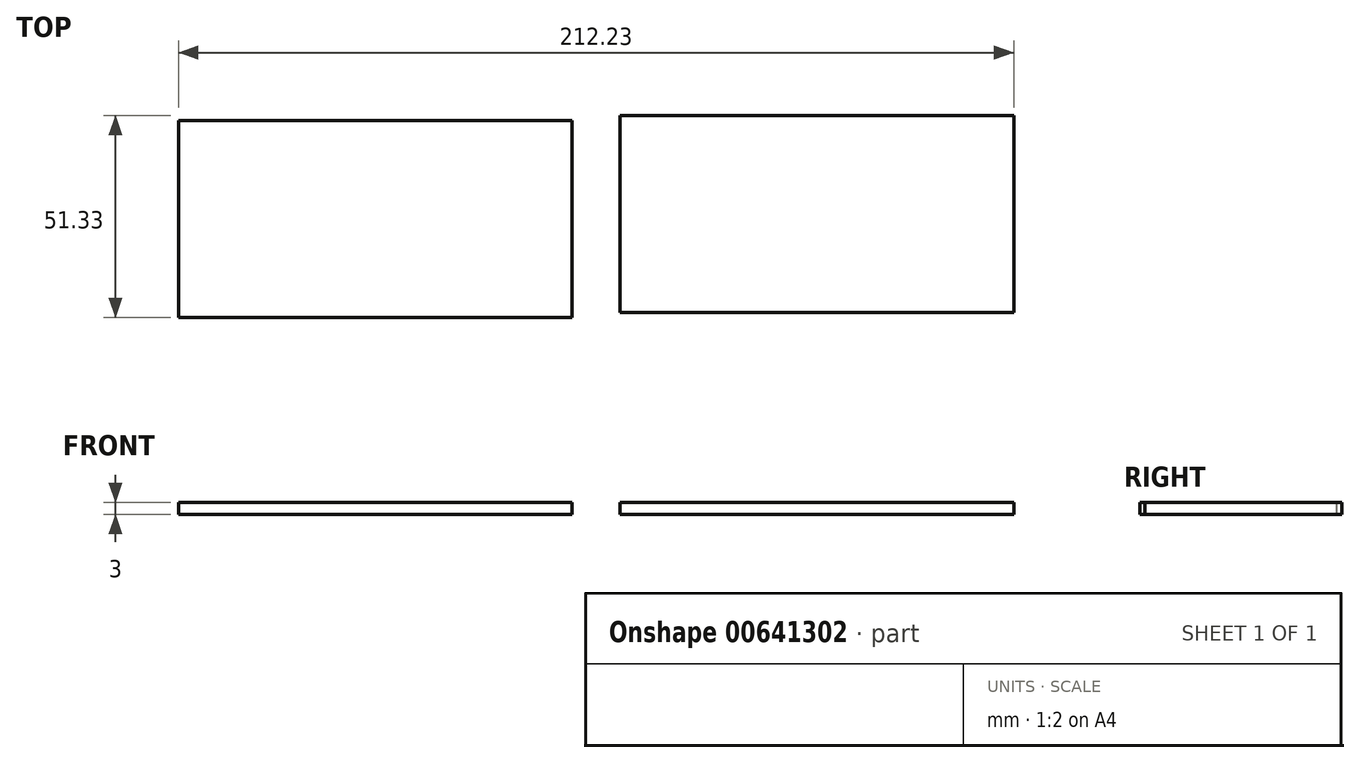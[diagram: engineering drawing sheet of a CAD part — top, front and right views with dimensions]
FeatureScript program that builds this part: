
annotation { "Feature Type Name" : "Feature", "Feature Type Description" : "" }
export const myFeature = defineFeature(function(context is Context, id is Id, definition is map)
    precondition{}
    {
        {
            var Q0;
            Q0=qCreatedBy(makeId("Top.planeOp"),FACE);
            var sketch = newSketch(context, id + "F0", { "sketchPlane" : qUnion([Q0])});
            skLineSegment(sketch, "E0.bottom", {"start": v(0, 0) * mm, "end": v(-100, 0) * mm});
            skLineSegment(sketch, "E0.top", {"start": v(0, 50) * mm, "end": v(-100, 50) * mm});
            skLineSegment(sketch, "E0.left", {"start": v(0, 0) * mm, "end": v(0, 50) * mm});
            skLineSegment(sketch, "E0.right", {"start": v(-100, 0) * mm, "end": v(-100, 50) * mm});
            skLineSegment(sketch, "E1.bottom", {"start": v(12.23, 1.33) * mm, "end": v(112.23, 1.33) * mm});
            skLineSegment(sketch, "E1.top", {"start": v(12.23, 51.33) * mm, "end": v(112.23, 51.33) * mm});
            skLineSegment(sketch, "E1.left", {"start": v(12.23, 1.33) * mm, "end": v(12.23, 51.33) * mm});
            skLineSegment(sketch, "E1.right", {"start": v(112.23, 1.33) * mm, "end": v(112.23, 51.33) * mm});
            skLineSegment(sketch, "E2.bottom", {"start": v(-28.72, -4.26) * mm, "end": v(-28.72, -4.26) * mm});
            skLineSegment(sketch, "E2.top", {"start": v(-28.72, -4.26) * mm, "end": v(-28.72, -4.26) * mm});
            skLineSegment(sketch, "E2.left", {"start": v(-28.72, -4.26) * mm, "end": v(-28.72, -4.26) * mm});
            skLineSegment(sketch, "E2.right", {"start": v(-28.72, -4.26) * mm, "end": v(-28.72, -4.26) * mm});
            skSolve(sketch);
        }
        {
            var Q0;
            Q0 = qSketchRegion(id + "F0", true);
            extrude(context, id + "F1", {"entities" : qUnion([Q0]), "depth" : 3 * mm, "offsetDistance" : 25 * mm});
        }
    });
